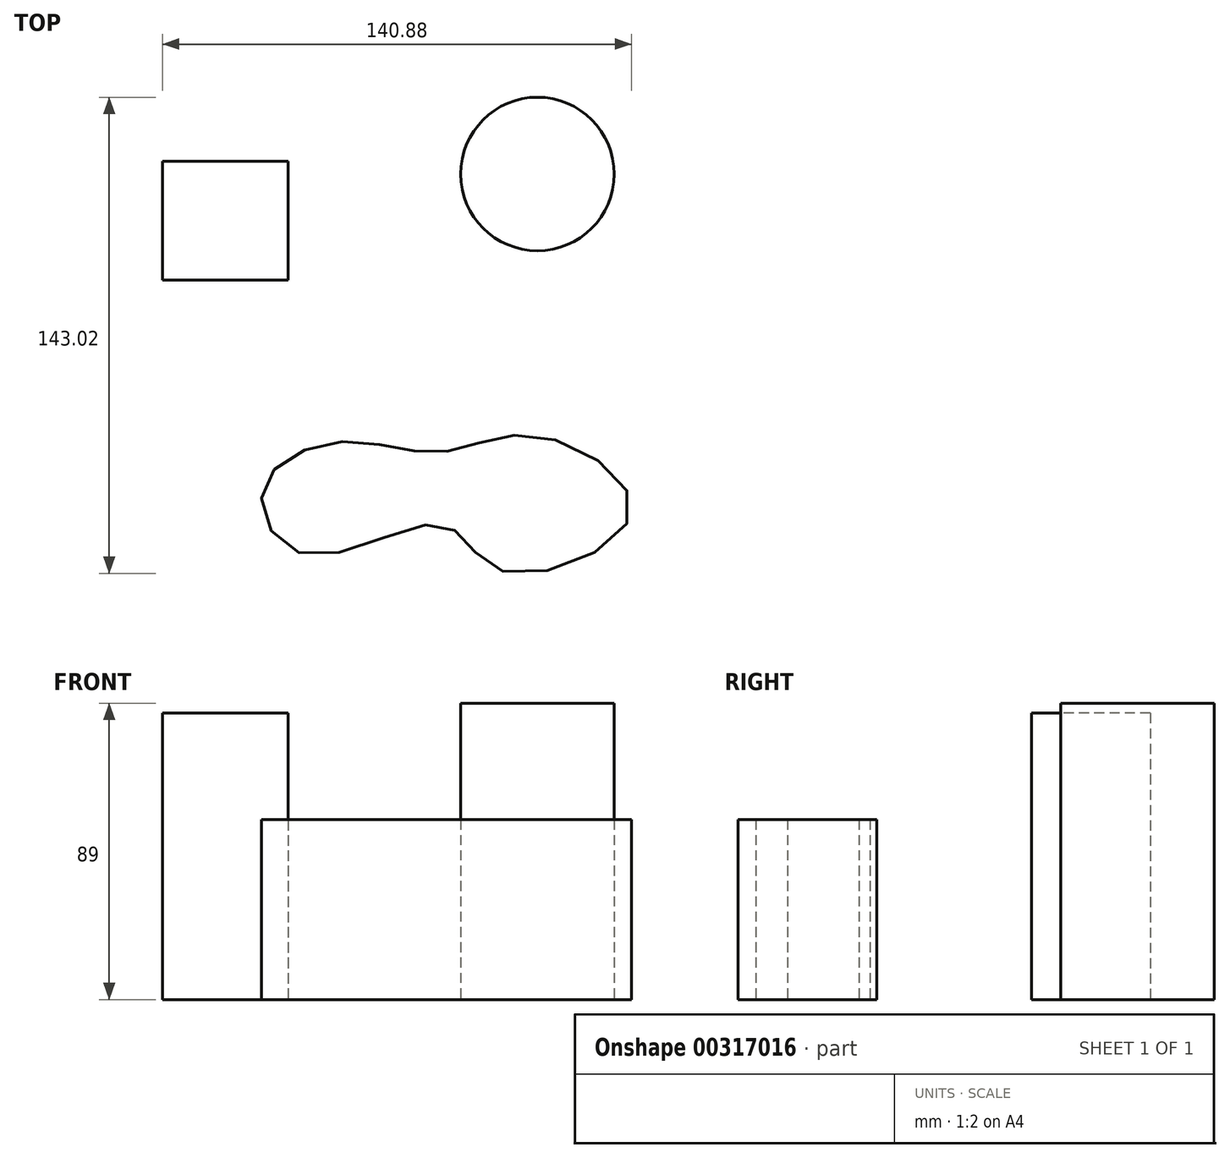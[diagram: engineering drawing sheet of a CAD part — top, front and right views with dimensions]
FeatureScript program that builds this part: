
annotation { "Feature Type Name" : "Feature", "Feature Type Description" : "" }
export const myFeature = defineFeature(function(context is Context, id is Id, definition is map)
    precondition{}
    {
        {
            var Q0;
            Q0=qCreatedBy(makeId("Top.planeOp"),FACE);
            var sketch = newSketch(context, id + "F0", { "sketchPlane" : qUnion([Q0])});
            skLineSegment(sketch, "E0.bottom", {"start": v(-93.92, 56.49) * mm, "end": v(-56.14, 56.49) * mm});
            skLineSegment(sketch, "E0.top", {"start": v(-93.92, 20.8) * mm, "end": v(-56.14, 20.8) * mm});
            skLineSegment(sketch, "E0.left", {"start": v(-93.92, 56.49) * mm, "end": v(-93.92, 20.8) * mm});
            skLineSegment(sketch, "E0.right", {"start": v(-56.14, 56.49) * mm, "end": v(-56.14, 20.8) * mm});
            skCircle(sketch, "E1", {"center": v(18.71, 52.68) * mm, "radius": 23.06 * mm});
            skFitSpline(sketch, "E2", {"points": [v(-39.85, -27.72) * mm, v(-63.77, -41.93) * mm, v(-50.6, -61.69) * mm, v(-9.7, -52.68) * mm, v(7.97, -66.54) * mm, v(46.78, -49.21) * mm, v(18.71, -26) * mm, v(-10.4, -30.84) * mm, v(-39.85, -27.72) * mm]});
            skSolve(sketch);
        }
        {
            var Q0;
            Q0=makeQuery(id+"F0.imprint","IMPRINT",FACE,{"disambiguationData":[TD([[makeQuery(id+"F0.imprint","IMPRINT",EDGE,{"derivedFrom":sQuery(id+"F0.wireOp",EDGE,"E2")}),1.0]])]});
            extrude(context, id + "F1", {"entities" : qUnion([Q0]), "depth" : 54 * mm});
        }
        {
            var Q0;
            Q0=makeQuery(id+"F0.imprint","IMPRINT",FACE,{"disambiguationData":[TD([[makeQuery(id+"F0.imprint","IMPRINT",EDGE,{"derivedFrom":sQuery(id+"F0.wireOp",EDGE,"E1")}),1.0]])]});
            extrude(context, id + "F2", {"entities" : qUnion([Q0]), "depth" : 89 * mm});
        }
        {
            var Q0;
            Q0=makeQuery(id+"F0.imprint","IMPRINT",FACE,{"disambiguationData":[TD([[makeQuery(id+"F0.imprint","IMPRINT",EDGE,{"derivedFrom":sQuery(id+"F0.wireOp",EDGE,"E0.bottom")}),-1.0]])]});
            extrude(context, id + "F3", {"entities" : qUnion([Q0]), "depth" : 86 * mm});
        }
        {
            var Q0;
            Q0=qCreatedBy(makeId("Front.planeOp"),FACE);
            var sketch = newSketch(context, id + "F4", { "sketchPlane" : qUnion([Q0])});
            skCircle(sketch, "E3", {"center": v(-27.54, 35.47) * mm, "radius": 13.4 * mm});
            skSolve(sketch);
        }
        {
            var Q0;
            Q0=sQuery(id+"F4.wireOp",EDGE,"E3");
            extrude(context, id + "F5", {"bodyType" : ToolBodyType.SURFACE, "surfaceEntities" : qUnion([Q0]), "depth" : 101 * mm});
        }
    });
